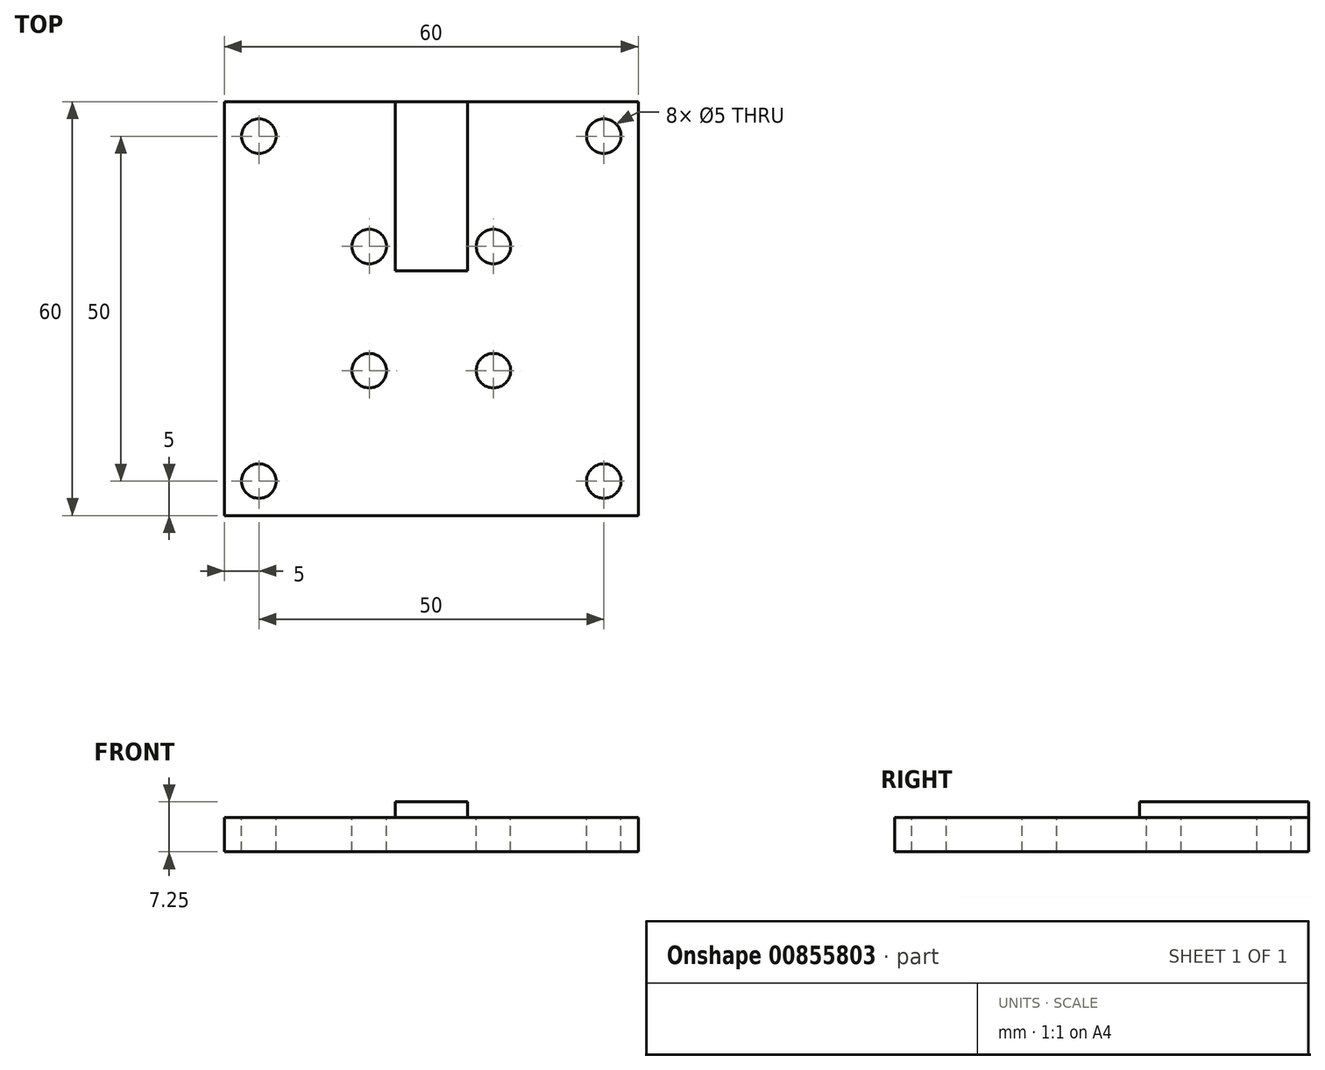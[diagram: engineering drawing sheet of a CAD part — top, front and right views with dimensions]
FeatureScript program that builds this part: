
annotation { "Feature Type Name" : "Feature", "Feature Type Description" : "" }
export const myFeature = defineFeature(function(context is Context, id is Id, definition is map)
    precondition{}
    {
        {
            var Q0;
            Q0=qCreatedBy(makeId("Top.planeOp"),FACE);
            var sketch = newSketch(context, id + "F0", { "sketchPlane" : qUnion([Q0])});
            skLineSegment(sketch, "E0.bottom", {"start": v(30, -30) * mm, "end": v(-30, -30) * mm});
            skLineSegment(sketch, "E0.top", {"start": v(30, 30) * mm, "end": v(-30, 30) * mm});
            skLineSegment(sketch, "E0.left", {"start": v(30, -30) * mm, "end": v(30, 30) * mm});
            skLineSegment(sketch, "E0.right", {"start": v(-30, -30) * mm, "end": v(-30, 30) * mm});
            skPoint(sketch, "E0.middle", {"position": v(0, 0) * mm});
            skLineSegment(sketch, "E1.bottom", {"start": v(9, -9) * mm, "end": v(-9, -9) * mm});
            skLineSegment(sketch, "E1.top", {"start": v(9, 9) * mm, "end": v(-9, 9) * mm});
            skLineSegment(sketch, "E1.left", {"start": v(9, -9) * mm, "end": v(9, 9) * mm});
            skLineSegment(sketch, "E1.right", {"start": v(-9, -9) * mm, "end": v(-9, 9) * mm});
            skCircle(sketch, "E2", {"center": v(-9, -9) * mm, "radius": 2.5 * mm});
            skCircle(sketch, "E3.MirrorC", {"center": v(9, -9) * mm, "radius": 2.5 * mm});
            skCircle(sketch, "E4.MirrorC", {"center": v(9, 9) * mm, "radius": 2.5 * mm});
            skCircle(sketch, "E5.MirrorC", {"center": v(-9, 9) * mm, "radius": 2.5 * mm});
            skLineSegment(sketch, "E6.bottom", {"start": v(25, -25) * mm, "end": v(-25, -25) * mm});
            skLineSegment(sketch, "E6.top", {"start": v(25, 25) * mm, "end": v(-25, 25) * mm});
            skLineSegment(sketch, "E6.left", {"start": v(25, -25) * mm, "end": v(25, 25) * mm});
            skLineSegment(sketch, "E6.right", {"start": v(-25, -25) * mm, "end": v(-25, 25) * mm});
            skCircle(sketch, "E7", {"center": v(-25, -25) * mm, "radius": 2.5 * mm});
            skCircle(sketch, "E8.MirrorC", {"center": v(25, -25) * mm, "radius": 2.5 * mm});
            skCircle(sketch, "E9.MirrorC", {"center": v(25, 25) * mm, "radius": 2.5 * mm});
            skCircle(sketch, "E10.MirrorC", {"center": v(-25, 25) * mm, "radius": 2.5 * mm});
            skLineSegment(sketch, "E11", {"start": v(5.25, -30) * mm, "end": v(30, -30) * mm});
            skLineSegment(sketch, "E12", {"start": v(0, -30) * mm, "end": v(5.25, -30) * mm});
            skSolve(sketch);
        }
        {
            var Q0;
            Q0=makeQuery(id+"F0.imprint","IMPRINT",FACE,{"disambiguationData":[TD([[makeQuery(id+"F0.imprint","IMPRINT",EDGE,{"derivedFrom":sQuery(id+"F0.wireOp",EDGE,"E0.bottom")}),-1.0]])]});
            var Q1;
            {var subQ14=sQuery(id+"F0.wireOp",EDGE,"E3.MirrorC");var subQ15=sQuery(id+"F0.wireOp",EDGE,"E1.bottom");var subQ16=makeQuery(id+"F0.imprint","INTERSECT",VERTEX,{"derivedFrom":[subQ15,subQ14]});Q1=makeQuery(id+"F0.imprint","IMPRINT",FACE,{"disambiguationData":[TD([[makeQuery(id+"F0.imprint","IMPRINT",EDGE,{"disambiguationData":[TD([[subQ16,-1.0]])],"derivedFrom":subQ15}),1.0]])]});}
            var Q2;
            {var subQ5=sQuery(id+"F0.wireOp",EDGE,"E3.MirrorC");var subQ13=sQuery(id+"F0.wireOp",EDGE,"E1.bottom");var subQ14=makeQuery(id+"F0.imprint","INTERSECT",VERTEX,{"derivedFrom":[subQ13,subQ5]});Q2=makeQuery(id+"F0.imprint","IMPRINT",FACE,{"disambiguationData":[TD([[makeQuery(id+"F0.imprint","IMPRINT",EDGE,{"disambiguationData":[TD([[subQ14,-1.0]])],"derivedFrom":subQ13}),-1.0]])]});}
            var Q3;
            Q3=makeQuery(id+"F0.imprint","IMPRINT",FACE,{"disambiguationData":[TD([[makeQuery(id+"F0.imprint","IMPRINT",EDGE,{"derivedFrom":sQuery(id+"F0.wireOp",EDGE,"fpgXcG0D-4lqi-jk3E-4btj-yLK3T1Owr0xt")}),1.0]])]});
            extrude(context, id + "F1", {"entities" : qUnion([Q0, Q1, Q2, Q3]), "oppositeDirection" : true, "depth" : 5 * mm, "offsetDistance" : 25 * mm});
        }
        {
            var Q0;
            Q0=makeQuery(id+"F1.opExtrude","CAP_FACE",FACE,{"disambiguationData":[OSD([sQuery(id+"F0.wireOp",EDGE,"E0.bottom"),sQuery(id+"F0.wireOp",EDGE,"E0.top"),sQuery(id+"F0.wireOp",EDGE,"E0.left"),sQuery(id+"F0.wireOp",EDGE,"E0.right"),sQuery(id+"F0.wireOp",EDGE,"E2"),sQuery(id+"F0.wireOp",EDGE,"E3.MirrorC"),sQuery(id+"F0.wireOp",EDGE,"E4.MirrorC"),sQuery(id+"F0.wireOp",EDGE,"E5.MirrorC"),sQuery(id+"F0.wireOp",EDGE,"E7"),sQuery(id+"F0.wireOp",EDGE,"E8.MirrorC"),sQuery(id+"F0.wireOp",EDGE,"E9.MirrorC"),sQuery(id+"F0.wireOp",EDGE,"E10.MirrorC")])],"isStart":true});
            var sketch = newSketch(context, id + "F2", { "sketchPlane" : qUnion([Q0])});
            skLineSegment(sketch, "E13.bottom", {"start": v(30, 30) * mm, "end": v(-30, 30) * mm});
            skLineSegment(sketch, "E13.top", {"start": v(30, -30) * mm, "end": v(-30, -30) * mm});
            skLineSegment(sketch, "E13.left", {"start": v(30, 30) * mm, "end": v(30, -30) * mm});
            skLineSegment(sketch, "E13.right", {"start": v(-30, 30) * mm, "end": v(-30, -30) * mm});
            skPoint(sketch, "E13.middle", {"position": v(0, 0) * mm});
            skLineSegment(sketch, "E14.bottom", {"start": v(5.25, 30) * mm, "end": v(-5.25, 30) * mm});
            skLineSegment(sketch, "E14.top", {"start": v(5.25, -30) * mm, "end": v(-5.25, -30) * mm});
            skLineSegment(sketch, "E14.left", {"start": v(5.25, 30) * mm, "end": v(5.25, -30) * mm});
            skLineSegment(sketch, "E14.right", {"start": v(-5.25, 30) * mm, "end": v(-5.25, -30) * mm});
            skLineSegment(sketch, "E15.bottom", {"start": v(30, 5.5) * mm, "end": v(-30, 5.5) * mm});
            skLineSegment(sketch, "E15.top", {"start": v(30, -5.5) * mm, "end": v(-30, -5.5) * mm});
            skLineSegment(sketch, "E15.left", {"start": v(30, 5.5) * mm, "end": v(30, -5.5) * mm});
            skLineSegment(sketch, "E15.right", {"start": v(-30, 5.5) * mm, "end": v(-30, -5.5) * mm});
            skSolve(sketch);
        }
        {
            var Q0;
            {var subQ0=sQuery(id+"F2.wireOp",EDGE,"E14.left");var subQ1=sQuery(id+"F2.wireOp",EDGE,"E13.bottom");var subQ2=makeQuery(id+"F2.imprint","INTERSECT",VERTEX,{"derivedFrom":[subQ1,subQ0]});Q0=makeQuery(id+"F2.imprint","IMPRINT",FACE,{"disambiguationData":[TD([[makeQuery(id+"F2.imprint","IMPRINT",EDGE,{"disambiguationData":[TD([[subQ2,-1.0]])],"derivedFrom":subQ1}),1.0]])]});}
            var Q1;
            {var subQ0=sQuery(id+"F2.wireOp",EDGE,"E14.top");Q1=makeQuery(id+"F2.imprint","IMPRINT",FACE,{"disambiguationData":[TD([[makeQuery(id+"F2.imprint","IMPRINT",EDGE,{"derivedFrom":subQ0}),-1.0]])]});}
            var Q2;
            {var subQ0=sQuery(id+"F2.wireOp",EDGE,"E14.right");var subQ1=sQuery(id+"F2.wireOp",EDGE,"E13.top");var subQ2=makeQuery(id+"F2.imprint","INTERSECT",VERTEX,{"derivedFrom":[subQ1,subQ0]});Q2=makeQuery(id+"F2.imprint","IMPRINT",FACE,{"disambiguationData":[TD([[makeQuery(id+"F2.imprint","IMPRINT",EDGE,{"disambiguationData":[TD([[subQ2,-1.0]])],"derivedFrom":subQ1}),1.0]])]});}
            extrude(context, id + "F3", {"entities" : qUnion([Q0, Q1, Q2]), "operationType" : NewBodyOperationType.ADD, "depth" : 2.25 * mm, "offsetDistance" : 25 * mm});
        }
    });
